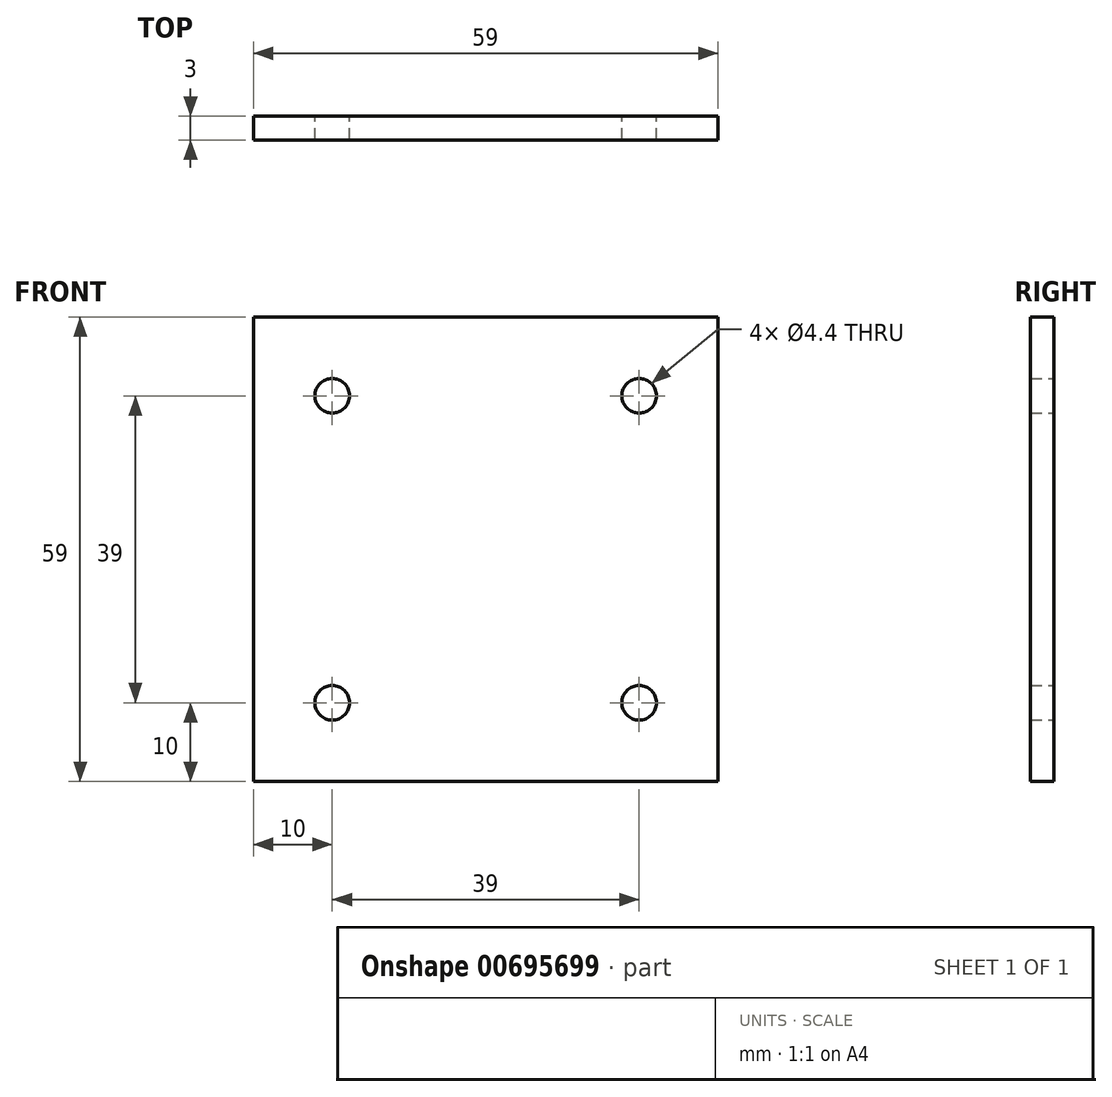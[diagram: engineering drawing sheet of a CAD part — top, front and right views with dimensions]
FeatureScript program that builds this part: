
annotation { "Feature Type Name" : "Feature", "Feature Type Description" : "" }
export const myFeature = defineFeature(function(context is Context, id is Id, definition is map)
    precondition{}
    {
        {
            var Q0;
            Q0=qCreatedBy(makeId("Front.planeOp"),FACE);
            var sketch = newSketch(context, id + "F0", { "sketchPlane" : qUnion([Q0])});
            skLineSegment(sketch, "E0.bottom", {"start": v(-29.5, 29.5) * mm, "end": v(29.5, 29.5) * mm});
            skLineSegment(sketch, "E0.top", {"start": v(-29.5, -29.5) * mm, "end": v(29.5, -29.5) * mm});
            skLineSegment(sketch, "E0.left", {"start": v(-29.5, 29.5) * mm, "end": v(-29.5, -29.5) * mm});
            skLineSegment(sketch, "E0.right", {"start": v(29.5, 29.5) * mm, "end": v(29.5, -29.5) * mm});
            skCircle(sketch, "E1", {"center": v(-19.5, 19.5) * mm, "radius": 2.2 * mm});
            skCircle(sketch, "E2.MirrorC", {"center": v(19.5, 19.5) * mm, "radius": 2.2 * mm});
            skCircle(sketch, "E3.MirrorC", {"center": v(-19.5, -19.5) * mm, "radius": 2.2 * mm});
            skCircle(sketch, "E4.MirrorC", {"center": v(19.5, -19.5) * mm, "radius": 2.2 * mm});
            skSolve(sketch);
        }
        {
            var Q0;
            Q0 = qSketchRegion(id + "F0", true);
            extrude(context, id + "F1", {"entities" : qUnion([Q0]), "depth" : 3 * mm, "offsetDistance" : 25 * mm});
        }
    });
